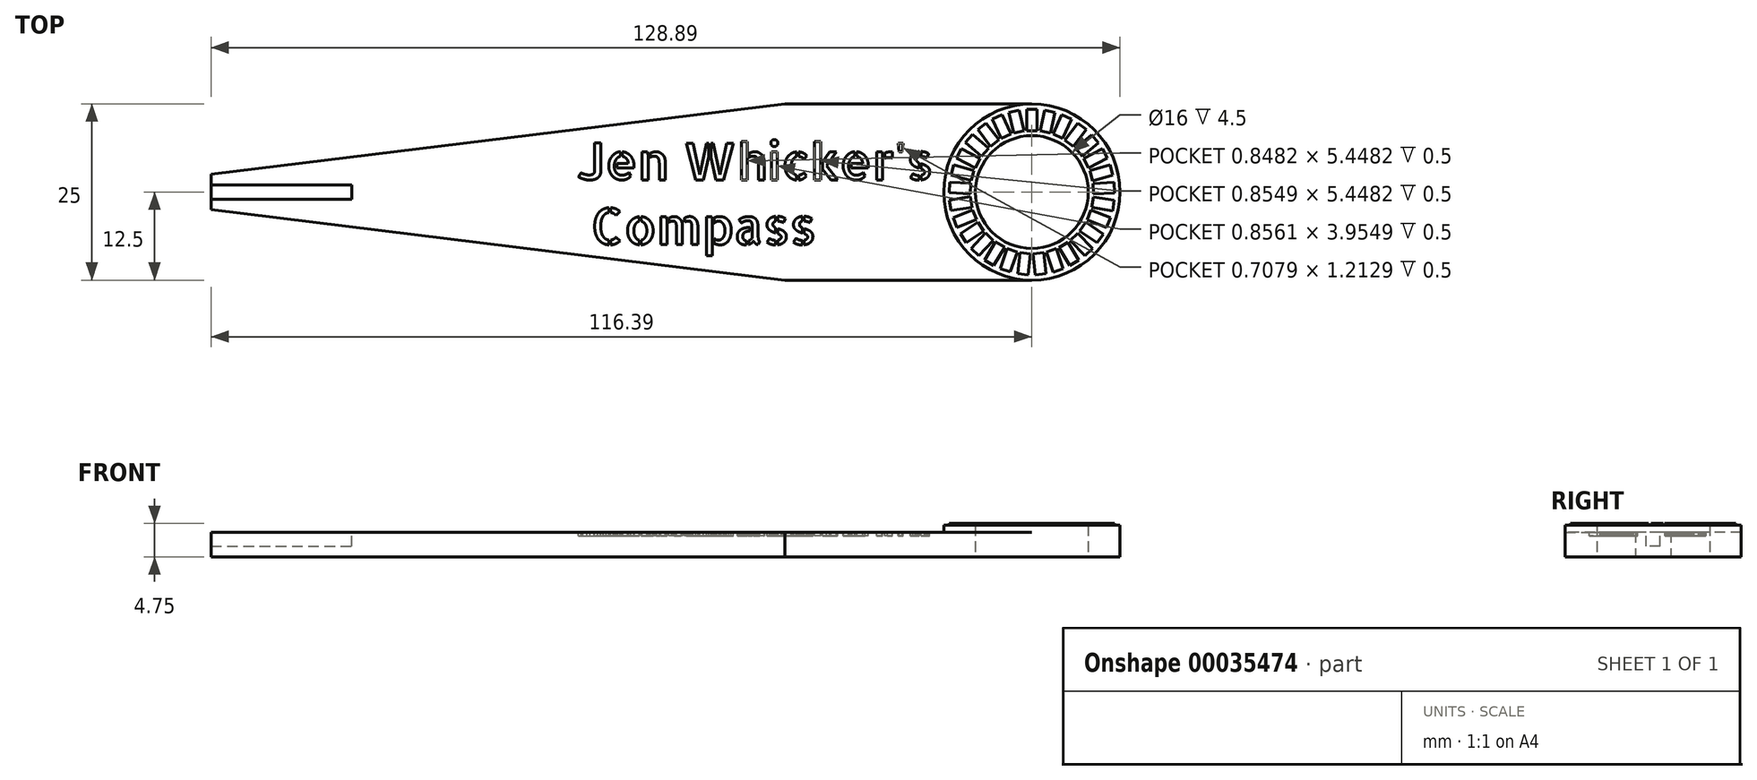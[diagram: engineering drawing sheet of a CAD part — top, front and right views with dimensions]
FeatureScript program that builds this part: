
annotation { "Feature Type Name" : "Feature", "Feature Type Description" : "" }
export const myFeature = defineFeature(function(context is Context, id is Id, definition is map)
    precondition{}
    {
        {
            var Q0;
            Q0=qCreatedBy(makeId("Top.planeOp"),FACE);
            var sketch = newSketch(context, id + "F0", { "sketchPlane" : qUnion([Q0])});
            skCircle(sketch, "E0", {"center": v(0, 0) * mm, "radius": 8 * mm});
            skCircle(sketch, "E1", {"center": v(0, 0) * mm, "radius": 12.5 * mm});
            skLineSegment(sketch, "E2", {"start": v(-35, 12.5) * mm, "end": v(0, 12.5) * mm});
            skLineSegment(sketch, "E3", {"start": v(-35, -12.5) * mm, "end": v(0, -12.5) * mm});
            skLineSegment(sketch, "E4", {"start": v(-35, 12.5) * mm, "end": v(-125, 12.5) * mm, "construction": true});
            skLineSegment(sketch, "E5", {"start": v(-35, 12.5) * mm, "end": v(-116.39, 2.5) * mm});
            skLineSegment(sketch, "E6", {"start": v(-35, -12.5) * mm, "end": v(-125, -12.5) * mm, "construction": true});
            skLineSegment(sketch, "E7", {"start": v(-35, -12.5) * mm, "end": v(-116.39, -2.5) * mm});
            skLineSegment(sketch, "E8", {"start": v(-116.39, 2.5) * mm, "end": v(-116.39, -2.5) * mm});
            skSolve(sketch);
        }
        {
            var Q0;
            Q0 = qSketchRegion(id + "F0", true);
            extrude(context, id + "F1", {"entities" : qUnion([Q0]), "depth" : 3.5 * mm});
        }
        {
            var Q0;
            Q0=makeQuery(id+"F1.opExtrude","CAP_FACE",FACE,{"disambiguationData":[OSD([sQuery(id+"F0.wireOp",EDGE,"E0"),sQuery(id+"F0.wireOp",EDGE,"E1"),sQuery(id+"F0.wireOp",EDGE,"E2"),sQuery(id+"F0.wireOp",EDGE,"E3"),sQuery(id+"F0.wireOp",EDGE,"E5"),sQuery(id+"F0.wireOp",EDGE,"E7"),sQuery(id+"F0.wireOp",EDGE,"E8")])],"isStart":false});
            var sketch = newSketch(context, id + "F2", { "sketchPlane" : qUnion([Q0])});
            skCircle(sketch, "E9", {"center": v(0, 0) * mm, "radius": 8 * mm});
            skSolve(sketch);
        }
        {
            var Q0;
            Q0=sQuery(id+"F0.wireOp",EDGE,"E1");
            var Q1;
            Q1=sQuery(id+"F2.wireOp",EDGE,"E9");
            extrude(context, id + "F3", {"bodyType" : ToolBodyType.SURFACE, "surfaceEntities" : qUnion([Q0, Q1]), "depth" : 1 * mm});
        }
        {
            var Q0;
            Q0=makeQuery(id+"F1.opExtrude","CAP_FACE",FACE,{"disambiguationData":[OSD([sQuery(id+"F0.wireOp",EDGE,"E0"),sQuery(id+"F0.wireOp",EDGE,"E1"),sQuery(id+"F0.wireOp",EDGE,"E2"),sQuery(id+"F0.wireOp",EDGE,"E3"),sQuery(id+"F0.wireOp",EDGE,"E5"),sQuery(id+"F0.wireOp",EDGE,"E7"),sQuery(id+"F0.wireOp",EDGE,"E8")])],"isStart":false});
            var sketch = newSketch(context, id + "F4", { "sketchPlane" : qUnion([Q0])});
            skLineSegment(sketch, "E10.bottom", {"start": v(-116.39, 1) * mm, "end": v(-96.39, 1) * mm});
            skLineSegment(sketch, "E10.top", {"start": v(-116.39, -1) * mm, "end": v(-96.39, -1) * mm});
            skLineSegment(sketch, "E10.left", {"start": v(-116.39, 1) * mm, "end": v(-116.39, -1) * mm});
            skLineSegment(sketch, "E10.right", {"start": v(-96.39, 1) * mm, "end": v(-96.39, -1) * mm});
            skSolve(sketch);
        }
        {
            var Q0;
            Q0=makeQuery(id+"F4.imprint","IMPRINT",FACE,{"disambiguationData":[TD([[makeQuery(id+"F4.imprint","IMPRINT",EDGE,{"derivedFrom":sQuery(id+"F4.wireOp",EDGE,"E10.bottom")}),-1.0]])]});
            extrude(context, id + "F5", {"entities" : qUnion([Q0]), "operationType" : NewBodyOperationType.REMOVE, "oppositeDirection" : true, "depth" : 2 * mm});
        }
        {
            var Q0;
            Q0=makeQuery(id+"F1.opExtrude","CAP_FACE",FACE,{"disambiguationData":[OSD([sQuery(id+"F0.wireOp",EDGE,"E0"),sQuery(id+"F0.wireOp",EDGE,"E1"),sQuery(id+"F0.wireOp",EDGE,"E2"),sQuery(id+"F0.wireOp",EDGE,"E3"),sQuery(id+"F0.wireOp",EDGE,"E5"),sQuery(id+"F0.wireOp",EDGE,"E7"),sQuery(id+"F0.wireOp",EDGE,"E8")])],"isStart":false});
            var sketch = newSketch(context, id + "F6", { "sketchPlane" : qUnion([Q0])});
            skCircle(sketch, "E11", {"center": v(0, 0) * mm, "radius": 8 * mm});
            skCircle(sketch, "E12", {"center": v(0, 0) * mm, "radius": 12.5 * mm});
            skSolve(sketch);
        }
        {
            var Q0;
            Q0=makeQuery(id+"F6.imprint","IMPRINT",FACE,{"disambiguationData":[TD([[makeQuery(id+"F6.imprint","IMPRINT",EDGE,{"derivedFrom":sQuery(id+"F6.wireOp",EDGE,"E11")}),-1.0]])]});
            extrude(context, id + "F7", {"entities" : qUnion([Q0]), "operationType" : NewBodyOperationType.ADD, "depth" : 1 * mm});
        }
        {
            var Q0;
            Q0=makeQuery(id+"F7.opExtrude","CAP_FACE",FACE,{"disambiguationData":[OSD([sQuery(id+"F6.wireOp",EDGE,"E11"),sQuery(id+"F6.wireOp",EDGE,"E12")])],"isStart":false});
            var sketch = newSketch(context, id + "F8", { "sketchPlane" : qUnion([Q0])});
            skLineSegment(sketch, "E13.bottom", {"start": v(-0.74, 11.72) * mm, "end": v(0.76, 11.72) * mm});
            skLineSegment(sketch, "E13.top", {"start": v(-0.74, 8.72) * mm, "end": v(0.76, 8.72) * mm});
            skLineSegment(sketch, "E13.left", {"start": v(-0.74, 11.72) * mm, "end": v(-0.74, 8.72) * mm});
            skLineSegment(sketch, "E13.right", {"start": v(0.76, 11.72) * mm, "end": v(0.76, 8.72) * mm});
            skLineSegment(sketch, "E14.1.0", {"start": v(1.8, 11.6) * mm, "end": v(1.16, 8.67) * mm});
            skLineSegment(sketch, "E14.1.1", {"start": v(1.16, 8.67) * mm, "end": v(2.62, 8.35) * mm});
            skLineSegment(sketch, "E14.1.2", {"start": v(3.27, 11.28) * mm, "end": v(2.62, 8.35) * mm});
            skLineSegment(sketch, "E14.1.3", {"start": v(1.8, 11.6) * mm, "end": v(3.27, 11.28) * mm});
            skLineSegment(sketch, "E14.2.0", {"start": v(4.25, 10.94) * mm, "end": v(3, 8.22) * mm});
            skLineSegment(sketch, "E14.2.1", {"start": v(3, 8.22) * mm, "end": v(4.35, 7.6) * mm});
            skLineSegment(sketch, "E14.2.2", {"start": v(5.61, 10.31) * mm, "end": v(4.35, 7.6) * mm});
            skLineSegment(sketch, "E14.2.3", {"start": v(4.25, 10.94) * mm, "end": v(5.61, 10.31) * mm});
            skLineSegment(sketch, "E14.3.0", {"start": v(6.5, 9.77) * mm, "end": v(4.7, 7.39) * mm});
            skLineSegment(sketch, "E14.3.1", {"start": v(4.7, 7.39) * mm, "end": v(5.88, 6.48) * mm});
            skLineSegment(sketch, "E14.3.2", {"start": v(7.7, 8.87) * mm, "end": v(5.88, 6.48) * mm});
            skLineSegment(sketch, "E14.3.3", {"start": v(6.5, 9.77) * mm, "end": v(7.7, 8.87) * mm});
            skLineSegment(sketch, "E14.4.0", {"start": v(8.46, 8.15) * mm, "end": v(6.17, 6.2) * mm});
            skLineSegment(sketch, "E14.4.1", {"start": v(6.17, 6.2) * mm, "end": v(7.14, 5.06) * mm});
            skLineSegment(sketch, "E14.4.2", {"start": v(9.43, 7) * mm, "end": v(7.14, 5.06) * mm});
            skLineSegment(sketch, "E14.4.3", {"start": v(8.46, 8.15) * mm, "end": v(9.43, 7) * mm});
            skLineSegment(sketch, "E14.5.0", {"start": v(10, 6.14) * mm, "end": v(7.36, 4.73) * mm});
            skLineSegment(sketch, "E14.5.1", {"start": v(7.36, 4.73) * mm, "end": v(8.06, 3.4) * mm});
            skLineSegment(sketch, "E14.5.2", {"start": v(10.71, 4.81) * mm, "end": v(8.06, 3.4) * mm});
            skLineSegment(sketch, "E14.5.3", {"start": v(10, 6.14) * mm, "end": v(10.71, 4.81) * mm});
            skLineSegment(sketch, "E14.6.0", {"start": v(11.1, 3.84) * mm, "end": v(8.2, 3.04) * mm});
            skLineSegment(sketch, "E14.6.1", {"start": v(8.2, 3.04) * mm, "end": v(8.6, 1.6) * mm});
            skLineSegment(sketch, "E14.6.2", {"start": v(11.5, 2.4) * mm, "end": v(8.6, 1.6) * mm});
            skLineSegment(sketch, "E14.6.3", {"start": v(11.1, 3.84) * mm, "end": v(11.5, 2.4) * mm});
            skLineSegment(sketch, "E14.7.0", {"start": v(11.66, 1.37) * mm, "end": v(8.67, 1.2) * mm});
            skLineSegment(sketch, "E14.7.1", {"start": v(8.67, 1.2) * mm, "end": v(8.75, -0.3) * mm});
            skLineSegment(sketch, "E14.7.2", {"start": v(11.74, -0.13) * mm, "end": v(8.75, -0.3) * mm});
            skLineSegment(sketch, "E14.7.3", {"start": v(11.66, 1.37) * mm, "end": v(11.74, -0.13) * mm});
            skLineSegment(sketch, "E14.8.0", {"start": v(11.68, -1.17) * mm, "end": v(8.72, -0.68) * mm});
            skLineSegment(sketch, "E14.8.1", {"start": v(8.72, -0.68) * mm, "end": v(8.48, -2.16) * mm});
            skLineSegment(sketch, "E14.8.2", {"start": v(11.44, -2.65) * mm, "end": v(8.48, -2.16) * mm});
            skLineSegment(sketch, "E14.8.3", {"start": v(11.68, -1.17) * mm, "end": v(11.44, -2.65) * mm});
            skLineSegment(sketch, "E14.9.0", {"start": v(11.16, -3.65) * mm, "end": v(8.37, -2.54) * mm});
            skLineSegment(sketch, "E14.9.1", {"start": v(8.37, -2.54) * mm, "end": v(7.82, -3.94) * mm});
            skLineSegment(sketch, "E14.9.2", {"start": v(10.6, -5.05) * mm, "end": v(7.82, -3.94) * mm});
            skLineSegment(sketch, "E14.9.3", {"start": v(11.16, -3.65) * mm, "end": v(10.6, -5.05) * mm});
            skLineSegment(sketch, "E14.10.0", {"start": v(10.11, -5.97) * mm, "end": v(7.63, -4.28) * mm});
            skLineSegment(sketch, "E14.10.1", {"start": v(7.63, -4.28) * mm, "end": v(6.79, -5.53) * mm});
            skLineSegment(sketch, "E14.10.2", {"start": v(9.27, -7.2) * mm, "end": v(6.79, -5.53) * mm});
            skLineSegment(sketch, "E14.10.3", {"start": v(10.11, -5.97) * mm, "end": v(9.27, -7.2) * mm});
            skLineSegment(sketch, "E14.11.0", {"start": v(8.6, -8) * mm, "end": v(6.53, -5.82) * mm});
            skLineSegment(sketch, "E14.11.1", {"start": v(6.53, -5.82) * mm, "end": v(5.44, -6.86) * mm});
            skLineSegment(sketch, "E14.11.2", {"start": v(7.5, -9.03) * mm, "end": v(5.44, -6.86) * mm});
            skLineSegment(sketch, "E14.11.3", {"start": v(8.6, -8) * mm, "end": v(7.5, -9.03) * mm});
            skLineSegment(sketch, "E14.12.0", {"start": v(6.67, -9.66) * mm, "end": v(5.13, -7.1) * mm});
            skLineSegment(sketch, "E14.12.1", {"start": v(5.13, -7.1) * mm, "end": v(3.84, -7.86) * mm});
            skLineSegment(sketch, "E14.12.2", {"start": v(5.39, -10.44) * mm, "end": v(3.84, -7.86) * mm});
            skLineSegment(sketch, "E14.12.3", {"start": v(6.67, -9.66) * mm, "end": v(5.39, -10.44) * mm});
            skLineSegment(sketch, "E14.13.0", {"start": v(4.44, -10.87) * mm, "end": v(3.48, -8.03) * mm});
            skLineSegment(sketch, "E14.13.1", {"start": v(3.48, -8.03) * mm, "end": v(2.06, -8.5) * mm});
            skLineSegment(sketch, "E14.13.2", {"start": v(3.02, -11.35) * mm, "end": v(2.06, -8.5) * mm});
            skLineSegment(sketch, "E14.13.3", {"start": v(4.44, -10.87) * mm, "end": v(3.02, -11.35) * mm});
            skLineSegment(sketch, "E14.14.0", {"start": v(2, -11.57) * mm, "end": v(1.67, -8.59) * mm});
            skLineSegment(sketch, "E14.14.1", {"start": v(1.67, -8.59) * mm, "end": v(0.18, -8.75) * mm});
            skLineSegment(sketch, "E14.14.2", {"start": v(0.5, -11.73) * mm, "end": v(0.18, -8.75) * mm});
            skLineSegment(sketch, "E14.14.3", {"start": v(2, -11.57) * mm, "end": v(0.5, -11.73) * mm});
            skLineSegment(sketch, "E14.15.0", {"start": v(-0.54, -11.73) * mm, "end": v(-0.21, -8.75) * mm});
            skLineSegment(sketch, "E14.15.1", {"start": v(-0.21, -8.75) * mm, "end": v(-1.7, -8.59) * mm});
            skLineSegment(sketch, "E14.15.2", {"start": v(-2.03, -11.57) * mm, "end": v(-1.7, -8.59) * mm});
            skLineSegment(sketch, "E14.15.3", {"start": v(-0.54, -11.73) * mm, "end": v(-2.03, -11.57) * mm});
            skLineSegment(sketch, "E14.16.0", {"start": v(-3.04, -11.34) * mm, "end": v(-2.09, -8.5) * mm});
            skLineSegment(sketch, "E14.16.1", {"start": v(-2.09, -8.5) * mm, "end": v(-3.5, -8.02) * mm});
            skLineSegment(sketch, "E14.16.2", {"start": v(-4.47, -10.86) * mm, "end": v(-3.5, -8.02) * mm});
            skLineSegment(sketch, "E14.16.3", {"start": v(-3.04, -11.34) * mm, "end": v(-4.47, -10.86) * mm});
            skLineSegment(sketch, "E14.17.0", {"start": v(-5.41, -10.42) * mm, "end": v(-3.86, -7.85) * mm});
            skLineSegment(sketch, "E14.17.1", {"start": v(-3.86, -7.85) * mm, "end": v(-5.15, -7.08) * mm});
            skLineSegment(sketch, "E14.17.2", {"start": v(-6.7, -9.65) * mm, "end": v(-5.15, -7.08) * mm});
            skLineSegment(sketch, "E14.17.3", {"start": v(-5.41, -10.42) * mm, "end": v(-6.7, -9.65) * mm});
            skLineSegment(sketch, "E14.18.0", {"start": v(-7.53, -9.01) * mm, "end": v(-5.46, -6.84) * mm});
            skLineSegment(sketch, "E14.18.1", {"start": v(-5.46, -6.84) * mm, "end": v(-6.55, -5.8) * mm});
            skLineSegment(sketch, "E14.18.2", {"start": v(-8.61, -7.98) * mm, "end": v(-6.55, -5.8) * mm});
            skLineSegment(sketch, "E14.18.3", {"start": v(-7.53, -9.01) * mm, "end": v(-8.61, -7.98) * mm});
            skLineSegment(sketch, "E14.19.0", {"start": v(-9.29, -7.19) * mm, "end": v(-6.8, -5.5) * mm});
            skLineSegment(sketch, "E14.19.1", {"start": v(-6.8, -5.5) * mm, "end": v(-7.65, -4.26) * mm});
            skLineSegment(sketch, "E14.19.2", {"start": v(-10.13, -5.94) * mm, "end": v(-7.65, -4.26) * mm});
            skLineSegment(sketch, "E14.19.3", {"start": v(-9.29, -7.19) * mm, "end": v(-10.13, -5.94) * mm});
            skLineSegment(sketch, "E14.20.0", {"start": v(-10.61, -5.02) * mm, "end": v(-7.83, -3.91) * mm});
            skLineSegment(sketch, "E14.20.1", {"start": v(-7.83, -3.91) * mm, "end": v(-8.38, -2.52) * mm});
            skLineSegment(sketch, "E14.20.2", {"start": v(-11.17, -3.63) * mm, "end": v(-8.38, -2.52) * mm});
            skLineSegment(sketch, "E14.20.3", {"start": v(-10.61, -5.02) * mm, "end": v(-11.17, -3.63) * mm});
            skLineSegment(sketch, "E14.21.0", {"start": v(-11.45, -2.62) * mm, "end": v(-8.49, -2.14) * mm});
            skLineSegment(sketch, "E14.21.1", {"start": v(-8.49, -2.14) * mm, "end": v(-8.73, -0.66) * mm});
            skLineSegment(sketch, "E14.21.2", {"start": v(-11.69, -1.14) * mm, "end": v(-8.73, -0.66) * mm});
            skLineSegment(sketch, "E14.21.3", {"start": v(-11.45, -2.62) * mm, "end": v(-11.69, -1.14) * mm});
            skLineSegment(sketch, "E14.22.0", {"start": v(-11.74, -0.1) * mm, "end": v(-8.75, -0.26) * mm});
            skLineSegment(sketch, "E14.22.1", {"start": v(-8.75, -0.26) * mm, "end": v(-8.66, 1.24) * mm});
            skLineSegment(sketch, "E14.22.2", {"start": v(-11.66, 1.4) * mm, "end": v(-8.66, 1.24) * mm});
            skLineSegment(sketch, "E14.22.3", {"start": v(-11.74, -0.1) * mm, "end": v(-11.66, 1.4) * mm});
            skLineSegment(sketch, "E14.23.0", {"start": v(-11.49, 2.43) * mm, "end": v(-8.6, 1.62) * mm});
            skLineSegment(sketch, "E14.23.1", {"start": v(-8.6, 1.62) * mm, "end": v(-8.2, 3.07) * mm});
            skLineSegment(sketch, "E14.23.2", {"start": v(-11.09, 3.87) * mm, "end": v(-8.2, 3.07) * mm});
            skLineSegment(sketch, "E14.23.3", {"start": v(-11.49, 2.43) * mm, "end": v(-11.09, 3.87) * mm});
            skLineSegment(sketch, "E14.24.0", {"start": v(-10.7, 4.84) * mm, "end": v(-8.05, 3.43) * mm});
            skLineSegment(sketch, "E14.24.1", {"start": v(-8.05, 3.43) * mm, "end": v(-7.35, 4.76) * mm});
            skLineSegment(sketch, "E14.24.2", {"start": v(-10, 6.16) * mm, "end": v(-7.35, 4.76) * mm});
            skLineSegment(sketch, "E14.24.3", {"start": v(-10.7, 4.84) * mm, "end": v(-10, 6.16) * mm});
            skLineSegment(sketch, "E14.25.0", {"start": v(-9.4, 7.03) * mm, "end": v(-7.12, 5.08) * mm});
            skLineSegment(sketch, "E14.25.1", {"start": v(-7.12, 5.08) * mm, "end": v(-6.15, 6.23) * mm});
            skLineSegment(sketch, "E14.25.2", {"start": v(-8.44, 8.17) * mm, "end": v(-6.15, 6.23) * mm});
            skLineSegment(sketch, "E14.25.3", {"start": v(-9.4, 7.03) * mm, "end": v(-8.44, 8.17) * mm});
            skLineSegment(sketch, "E14.26.0", {"start": v(-7.68, 8.88) * mm, "end": v(-5.86, 6.5) * mm});
            skLineSegment(sketch, "E14.26.1", {"start": v(-5.86, 6.5) * mm, "end": v(-4.67, 7.4) * mm});
            skLineSegment(sketch, "E14.26.2", {"start": v(-6.48, 9.8) * mm, "end": v(-4.67, 7.4) * mm});
            skLineSegment(sketch, "E14.26.3", {"start": v(-7.68, 8.88) * mm, "end": v(-6.48, 9.8) * mm});
            skLineSegment(sketch, "E14.27.0", {"start": v(-5.59, 10.33) * mm, "end": v(-4.33, 7.6) * mm});
            skLineSegment(sketch, "E14.27.1", {"start": v(-4.33, 7.6) * mm, "end": v(-2.97, 8.23) * mm});
            skLineSegment(sketch, "E14.27.2", {"start": v(-4.23, 10.96) * mm, "end": v(-2.97, 8.23) * mm});
            skLineSegment(sketch, "E14.27.3", {"start": v(-5.59, 10.33) * mm, "end": v(-4.23, 10.96) * mm});
            skLineSegment(sketch, "E14.28.0", {"start": v(-3.24, 11.29) * mm, "end": v(-2.6, 8.36) * mm});
            skLineSegment(sketch, "E14.28.1", {"start": v(-2.6, 8.36) * mm, "end": v(-1.13, 8.68) * mm});
            skLineSegment(sketch, "E14.28.2", {"start": v(-1.77, 11.6) * mm, "end": v(-1.13, 8.68) * mm});
            skLineSegment(sketch, "E14.28.3", {"start": v(-3.24, 11.29) * mm, "end": v(-1.77, 11.6) * mm});
            skPoint(sketch, "E14.center", {"position": v(0, 0) * mm});
            skLineSegment(sketch, "E14.anchor1", {"start": v(0, 0) * mm, "end": v(-0.74, 8.72) * mm, "construction": true});
            skLineSegment(sketch, "E14.anchor2", {"start": v(0, 0) * mm, "end": v(-0.74, 8.72) * mm, "construction": true});
            skSolve(sketch);
        }
        {
            var Q0;
            Q0 = qSketchRegion(id + "F8", true);
            extrude(context, id + "F9", {"entities" : qUnion([Q0]), "operationType" : NewBodyOperationType.ADD, "depth" : .25 * mm});
        }
        {
            var Q0;
            Q0=makeQuery(id+"F1.opExtrude","CAP_FACE",FACE,{"disambiguationData":[OSD([sQuery(id+"F0.wireOp",EDGE,"E0"),sQuery(id+"F0.wireOp",EDGE,"E1"),sQuery(id+"F0.wireOp",EDGE,"E2"),sQuery(id+"F0.wireOp",EDGE,"E3"),sQuery(id+"F0.wireOp",EDGE,"E5"),sQuery(id+"F0.wireOp",EDGE,"E7"),sQuery(id+"F0.wireOp",EDGE,"E8")])],"isStart":false});
            var sketch = newSketch(context, id + "F10", { "sketchPlane" : qUnion([Q0])});
            skText(sketch, "E15", { "text": "Jen Whicker\'s\n Compass", "fontName": "AllertaStencil-Regular.ttf"});
            const initialGuessF10  = {"E15": [-0.06446, 0.00173, 1, 0, 0.00517]};
            skSetInitialGuess(sketch, initialGuessF10);
            skSolve(sketch);
        }
        {
            var Q0;
            Q0 = qSketchRegion(id + "F10", true);
            extrude(context, id + "F11", {"entities" : qUnion([Q0]), "operationType" : NewBodyOperationType.REMOVE, "oppositeDirection" : true, "depth" : .5 * mm});
        }
    });
